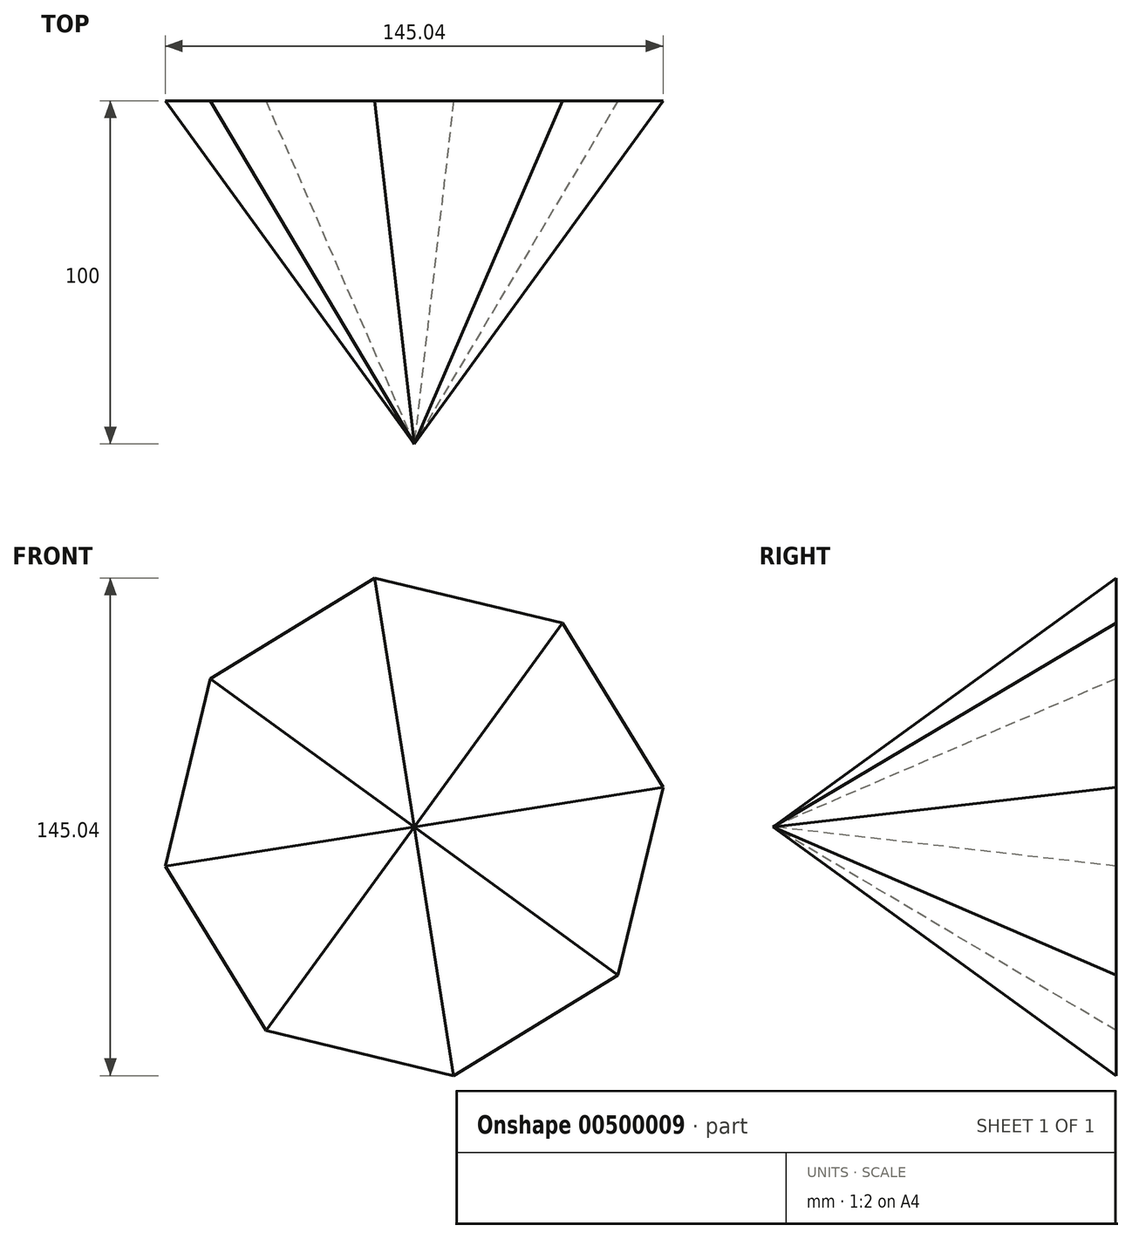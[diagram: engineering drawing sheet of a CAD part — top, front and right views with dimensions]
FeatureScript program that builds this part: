
annotation { "Feature Type Name" : "Feature", "Feature Type Description" : "" }
export const myFeature = defineFeature(function(context is Context, id is Id, definition is map)
    precondition{}
    {
        {
            var Q0;
            Q0=qCreatedBy(makeId("Front.planeOp"),FACE);
            var sketch = newSketch(context, id + "F0", { "sketchPlane" : qUnion([Q0])});
            skCircle(sketch, "E0.cCircle", {"center": v(0, 0) * mm, "radius": 73.42 * mm, "construction": true});
            skLineSegment(sketch, "E0.0", {"start": v(-59.39, 43.18) * mm, "end": v(-11.46, 72.52) * mm});
            skLineSegment(sketch, "E0.1", {"start": v(-11.46, 72.52) * mm, "end": v(43.18, 59.39) * mm});
            skLineSegment(sketch, "E0.2", {"start": v(43.18, 59.39) * mm, "end": v(72.52, 11.46) * mm});
            skLineSegment(sketch, "E0.3", {"start": v(72.52, 11.46) * mm, "end": v(59.39, -43.18) * mm});
            skLineSegment(sketch, "E0.4", {"start": v(59.39, -43.18) * mm, "end": v(11.46, -72.52) * mm});
            skLineSegment(sketch, "E0.5", {"start": v(11.46, -72.52) * mm, "end": v(-43.18, -59.39) * mm});
            skLineSegment(sketch, "E0.6", {"start": v(-43.18, -59.39) * mm, "end": v(-72.52, -11.46) * mm});
            skLineSegment(sketch, "E0.7", {"start": v(-72.52, -11.46) * mm, "end": v(-59.39, 43.18) * mm});
            skSolve(sketch);
        }
        {
            var Q0;
            Q0=qCreatedBy(makeId("Front.planeOp"),FACE);
            cPlane(context, id + "F1", {"entities" : qUnion([Q0]), "cplaneType" : CPlaneType.OFFSET, "offset" : 100 * mm, "width" : 150 * mm, "height" : 150 * mm});
        }
        {
            var Q0;
            Q0=qCreatedBy(id+"F1.planeOp",FACE);
            var sketch = newSketch(context, id + "F2", { "sketchPlane" : qUnion([Q0])});
            skPoint(sketch, "E1", {"position": v(0, 0) * mm});
            skSolve(sketch);
        }
        {
            var Q0;
            Q0=makeQuery(id+"F0.imprint","IMPRINT",FACE,{"disambiguationData":[TD([[makeQuery(id+"F0.imprint","IMPRINT",EDGE,{"derivedFrom":sQuery(id+"F0.wireOp",EDGE,"E0.0")}),-1.0]])]});
            var Q1;
            Q1=sQuery(id+"F2.wireOp",VERTEX,"E1");
            loft(context, id + "F3", {"sheetProfilesArray" : [{ "sheetProfileEntities" : qUnion([Q0]) }, { "sheetProfileEntities" : qUnion([Q1]) }]});
        }
    });
